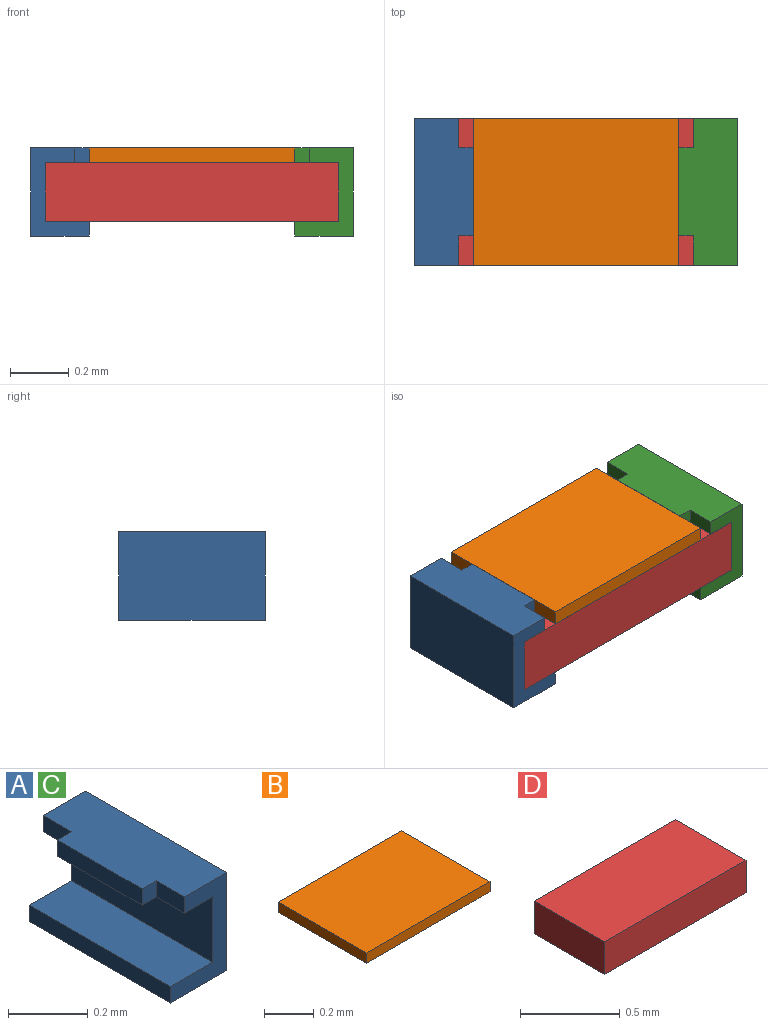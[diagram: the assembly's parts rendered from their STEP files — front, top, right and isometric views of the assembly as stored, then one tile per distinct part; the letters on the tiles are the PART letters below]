
ASSEMBLY  parts=4 mates=3
PART A: 14 faces, bbox 0.2x0.5x0.3 mm
  f0: plane 0.1x0.05mm, normal (-1,0,0), area 0mm2, adj f4,f6,f9,f13
  f1: plane 0.5x0.05mm, normal (-1,0,0), area 0mm2, adj f2,f8,f9,f10
  f2: plane 0.5x0.2mm, normal (0,0,-1), area 0.1mm2, adj f1,f3,f9,f10
  f3: plane 0.5x0.3mm, normal (1,0,0), area 0.1mm2, adj f2,f4,f9,f10
  f4: plane 0.5x0.2mm, normal (0,0,1), area 0.1mm2, adj f0,f3,f5,f9,f10,f11,f12,f13
  f5: plane 0.1x0.05mm, normal (-1,0,0), area 0mm2, adj f4,f6,f10,f11
  f6: plane 0.5x0.15mm, normal (0,0,-1), area 0.1mm2, adj f0,f5,f7,f9,f10,f11,f12,f13
  f7: plane 0.5x0.2mm, normal (-1,0,0), area 0.1mm2, adj f6,f8,f9,f10
  f8: plane 0.5x0.15mm, normal (0,0,1), area 0.1mm2, adj f1,f7,f9,f10
  f9: plane 0.3x0.2mm, normal (0,-1,0), area 0mm2, adj f0,f1,f2,f3,f4,f6,f7,f8
  f10: plane 0.3x0.2mm, normal (0,1,0), area 0mm2, adj f1,f2,f3,f4,f5,f6,f7,f8
  f11: plane 0.05x0.05mm, normal (0,1,0), area 0mm2, adj f4,f5,f6,f12
  f12: plane 0.3x0.05mm, normal (-1,0,0), area 0mm2, adj f4,f6,f11,f13
  f13: plane 0.05x0.05mm, normal (0,-1,0), area 0mm2, adj f0,f4,f6,f12
PART B: 6 faces, bbox 0.7x0.5x0.1 mm
  f0: plane 0.7x0.05mm, normal (0,1,0), area 0mm2, adj f1,f3,f4,f5
  f1: plane 0.5x0.05mm, normal (-1,0,0), area 0mm2, adj f0,f2,f4,f5
  f2: plane 0.7x0.05mm, normal (0,-1,0), area 0mm2, adj f1,f3,f4,f5
  f3: plane 0.5x0.05mm, normal (1,0,0), area 0mm2, adj f0,f2,f4,f5
  f4: plane 0.7x0.5mm, normal (0,0,1), area 0.3mm2, adj f0,f1,f2,f3
  f5: plane 0.7x0.5mm, normal (0,0,-1), area 0.3mm2, adj f0,f1,f2,f3
PART C: same geometry as A
PART D: 6 faces, bbox 1x0.5x0.2 mm
  f0: plane 1x0.2mm, normal (0,1,0), area 0.2mm2, adj f1,f3,f4,f5
  f1: plane 0.5x0.2mm, normal (-1,0,0), area 0.1mm2, adj f0,f2,f4,f5
  f2: plane 1x0.2mm, normal (0,-1,0), area 0.2mm2, adj f1,f3,f4,f5
  f3: plane 0.5x0.2mm, normal (1,0,0), area 0.1mm2, adj f0,f2,f4,f5
  f4: plane 1x0.5mm, normal (0,0,1), area 0.5mm2, adj f0,f1,f2,f3
  f5: plane 1x0.5mm, normal (0,0,-1), area 0.5mm2, adj f0,f1,f2,f3
PLACE A rot(axis=(0,0,1),180deg) t=(0.29,-2.36,-0.43)mm
PLACE B t=(-2.82,-8.86,-0.18)mm
PLACE C t=(0.99,-1.86,-0.43)mm fixed
PLACE D t=(-4,0.51,-0.38)mm fixed
MATE fastened D.f1 <-> A.f7  axis (-1,0,0) through (0.14,-2.11,-0.28)mm
MATE fastened B.f5 <-> D.f4  axis (0,0,-1) through (0.64,-2.11,-0.18)mm
MATE fastened D.f3 <-> C.f7  axis (1,0,0) through (1.14,-2.11,-0.28)mm
